# Revit family: 603-A-4100-DN250
name_source: partatom
category: Pipe Accessories
units: mm (PartAtom-declared; Revit-internal decimal feet)

## family parameters
Always vertical = Yes
Cut with Voids When Loaded = No
Part Type = Valve - Breaks Into
Round Connector Dimension = Use Diameter
Shared = No
Work Plane-Based = No

## types (4) — shared parameters
Bolt_ref = 154 mm  [stored 0.505249 ft]
Bolt_width = 20 mm  [stored 0.0656168 ft]
Bottm_cut = 160 mm
Bottm_height = 7 mm  [stored 0.0229659 ft]
Bottom_Flange_Thicckness = 12 mm  [stored 0.0393701 ft]
D2 = 146 mm
D3 = 175 mm  [stored 0.574147 ft]
D4 = 197 mm  [stored 0.646325 ft]
DN250_ 280-306 = 603-306-000-4100
DN250_242-268 = 603-268-000-4100
DN250_266- 292 = 603-292-002-4100
DN250_266-292 = 603-292-000-4100
Description_ = AVK UNIVERSAL SUPA® FLANGE ADAPTOR
H1 = 35 mm  [stored 0.114829 ft]
ID = 125 mm  [stored 0.410105 ft]
L = 182 mm  [stored 0.597113 ft]
L1 = 58 mm  [stored 0.190289 ft]
L3 = 112 mm  [stored 0.367454 ft]
Length = 117 mm  [stored 0.383858 ft]
Nomianal_Diameter(DN) = 250 mm  [stored 0.82021 ft]
Nut = 10 mm  [stored 0.0328084 ft]
PCD = 370 mm  [stored 1.21391 ft]
Rib_Thickness = 5 mm  [stored 0.0164042 ft]
Rib_length = 32 mm  [stored 0.104987 ft]
Rib_width = 410 mm  [stored 1.34514 ft]
Search_table = 603-A-4100-DN250
URL product pages = https://www.avkvalves.com
Washer = 3 mm  [stored 0.00984252 ft]
Washer_ref = 144 mm  [stored 0.472441 ft]

## per-type parameters (varying)
| type | D |
| 603-268-000-4100_DN250 | 203 mm  [stored 0.66601 ft] |
| 603-292-000-4100_DN250 | 203 mm  [stored 0.66601 ft] |
| 603-292-002-4100_DN250 | 203 mm  [stored 0.66601 ft] |
| 603-306-000-4100_DN250 | 210 mm  [stored 0.688976 ft] |

note: [stored X ft] marks values corroborated as IEEE doubles in the binary element streams (Revit-internal decimal feet)

## geometry (parser evidence)
native form markers: Sweep x10
no freeform markers — native parametric forms only
